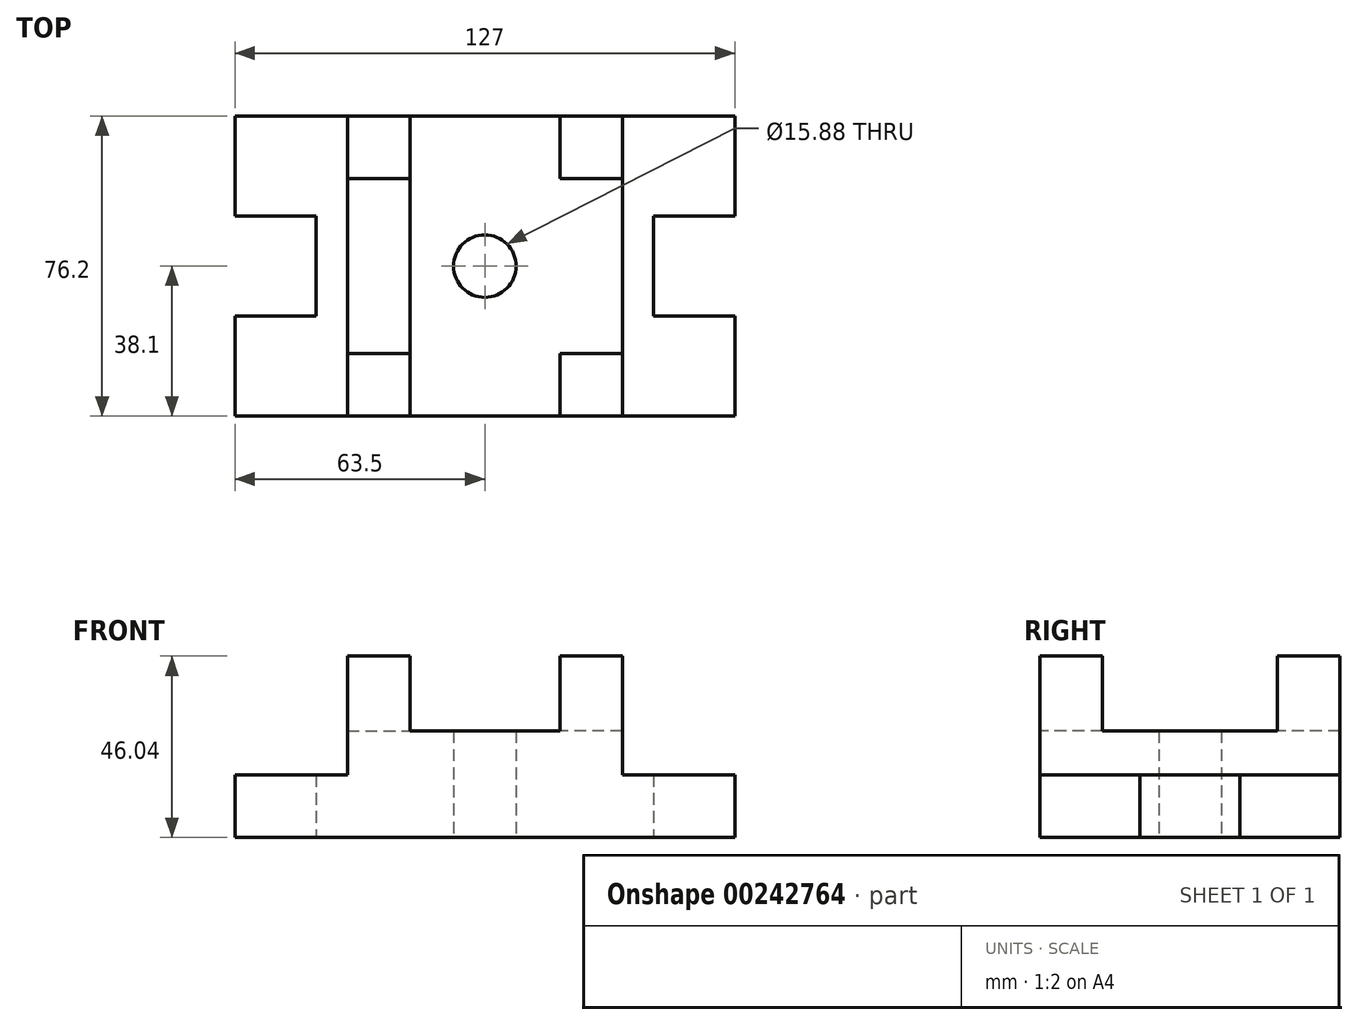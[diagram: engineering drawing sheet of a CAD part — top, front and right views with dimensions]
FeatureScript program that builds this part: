
annotation { "Feature Type Name" : "Feature", "Feature Type Description" : "" }
export const myFeature = defineFeature(function(context is Context, id is Id, definition is map)
    precondition{}
    {
        {
            var Q0;
            Q0=qCreatedBy(makeId("Top.planeOp"),FACE);
            var sketch = newSketch(context, id + "F0", { "sketchPlane" : qUnion([Q0])});
            skLineSegment(sketch, "E0.bottom", {"start": v(63.5, 38.1) * mm, "end": v(-63.5, 38.1) * mm});
            skLineSegment(sketch, "E0.top", {"start": v(63.5, -38.1) * mm, "end": v(-63.5, -38.1) * mm});
            skLineSegment(sketch, "E0.left", {"start": v(63.5, 38.1) * mm, "end": v(63.5, 12.7) * mm});
            skPoint(sketch, "E0.middle", {"position": v(0, 0) * mm});
            skLineSegment(sketch, "E1.bottom", {"start": v(-42.85, 12.7) * mm, "end": v(-63.5, 12.7) * mm});
            skLineSegment(sketch, "E1.top", {"start": v(-42.85, -12.7) * mm, "end": v(-63.5, -12.7) * mm});
            skLineSegment(sketch, "E1.left", {"start": v(-42.85, 12.7) * mm, "end": v(-42.85, -12.7) * mm});
            skPoint(sketch, "E1.middle", {"position": v(-53.17, 0) * mm});
            skLineSegment(sketch, "E2.bottom", {"start": v(63.5, 12.7) * mm, "end": v(42.85, 12.7) * mm});
            skLineSegment(sketch, "E2.top", {"start": v(63.5, -12.7) * mm, "end": v(42.85, -12.7) * mm});
            skPoint(sketch, "E2.middle", {"position": v(53.17, 0) * mm});
            skLineSegment(sketch, "E3", {"start": v(42.85, 12.7) * mm, "end": v(42.85, -12.7) * mm});
            skLineSegment(sketch, "E4.trimOffspring", {"start": v(63.5, -12.7) * mm, "end": v(63.5, -38.1) * mm});
            skLineSegment(sketch, "E5", {"start": v(-63.5, -12.7) * mm, "end": v(-63.5, -38.1) * mm});
            skLineSegment(sketch, "E6", {"start": v(-63.5, 38.1) * mm, "end": v(-63.5, 12.7) * mm});
            skSolve(sketch);
        }
        {
            var Q0;
            Q0=makeQuery(id+"F0.imprint","IMPRINT",FACE,{"disambiguationData":[TD([[makeQuery(id+"F0.imprint","IMPRINT",EDGE,{"derivedFrom":sQuery(id+"F0.wireOp",EDGE,"E0.bottom")}),1.0]])]});
            extrude(context, id + "F1", {"entities" : qUnion([Q0]), "depth" : 15.88 * mm});
        }
        {
            var Q0;
            Q0=makeQuery(id+"F1.opExtrude","CAP_FACE",FACE,{"disambiguationData":[OSD([sQuery(id+"F0.wireOp",EDGE,"E0.bottom"),sQuery(id+"F0.wireOp",EDGE,"E0.top"),sQuery(id+"F0.wireOp",EDGE,"E0.left"),sQuery(id+"F0.wireOp",EDGE,"E1.bottom"),sQuery(id+"F0.wireOp",EDGE,"E1.top"),sQuery(id+"F0.wireOp",EDGE,"E1.left"),sQuery(id+"F0.wireOp",EDGE,"E2.bottom"),sQuery(id+"F0.wireOp",EDGE,"E2.top"),sQuery(id+"F0.wireOp",EDGE,"E3"),sQuery(id+"F0.wireOp",EDGE,"E4.trimOffspring"),sQuery(id+"F0.wireOp",EDGE,"E5"),sQuery(id+"F0.wireOp",EDGE,"E6")])],"isStart":false});
            var sketch = newSketch(context, id + "F2", { "sketchPlane" : qUnion([Q0])});
            skLineSegment(sketch, "E7.bottom", {"start": v(34.93, 38.1) * mm, "end": v(-34.93, 38.1) * mm});
            skLineSegment(sketch, "E7.top", {"start": v(34.93, -38.1) * mm, "end": v(-34.92, -38.1) * mm});
            skLineSegment(sketch, "E7.left", {"start": v(34.93, 38.1) * mm, "end": v(34.93, -38.1) * mm});
            skLineSegment(sketch, "E7.right", {"start": v(-34.93, 38.1) * mm, "end": v(-34.92, -38.1) * mm});
            skPoint(sketch, "E7.middle", {"position": v(0, 0) * mm});
            skCircle(sketch, "E8", {"center": v(0, 0) * mm, "radius": 7.94 * mm});
            skSolve(sketch);
        }
        {
            var Q0;
            Q0=makeQuery(id+"F2.imprint","IMPRINT",FACE,{"disambiguationData":[TD([[makeQuery(id+"F2.imprint","IMPRINT",EDGE,{"derivedFrom":sQuery(id+"F2.wireOp",EDGE,"E7.bottom")}),1.0]])]});
            extrude(context, id + "F3", {"entities" : qUnion([Q0]), "operationType" : NewBodyOperationType.ADD, "depth" : 11.1 * mm});
        }
        {
            var Q0;
            Q0=makeQuery(id+"F3.boolean.opBoolean","SPLIT",FACE,{"disambiguationData":[TD([makeQuery(id+"F3.opExtrude","SWEPT_FACE",FACE,{"disambiguationData":[OSD([sQuery(id+"F2.wireOp",EDGE,"E8")])]})])],"derivedFrom":makeQuery(id+"F1.opExtrude","CAP_FACE",FACE,{"disambiguationData":[OSD([sQuery(id+"F0.wireOp",EDGE,"E0.bottom"),sQuery(id+"F0.wireOp",EDGE,"E0.top"),sQuery(id+"F0.wireOp",EDGE,"E0.left"),sQuery(id+"F0.wireOp",EDGE,"E1.bottom"),sQuery(id+"F0.wireOp",EDGE,"E1.top"),sQuery(id+"F0.wireOp",EDGE,"E1.left"),sQuery(id+"F0.wireOp",EDGE,"E2.bottom"),sQuery(id+"F0.wireOp",EDGE,"E2.top"),sQuery(id+"F0.wireOp",EDGE,"E3"),sQuery(id+"F0.wireOp",EDGE,"E4.trimOffspring"),sQuery(id+"F0.wireOp",EDGE,"E5"),sQuery(id+"F0.wireOp",EDGE,"E6")])],"isStart":false})});
            extrude(context, id + "F4", {"entities" : qUnion([Q0]), "operationType" : NewBodyOperationType.REMOVE, "endBound" : BoundingType.THROUGH_ALL, "oppositeDirection" : true, "depth" : 25.4 * mm});
        }
        {
            var Q0;
            Q0=makeQuery(id+"F3.opExtrude","CAP_FACE",FACE,{"disambiguationData":[OSD([sQuery(id+"F2.wireOp",EDGE,"E7.bottom"),sQuery(id+"F2.wireOp",EDGE,"E7.top"),sQuery(id+"F2.wireOp",EDGE,"E7.left"),sQuery(id+"F2.wireOp",EDGE,"E7.right"),sQuery(id+"F2.wireOp",EDGE,"E8")])],"isStart":false});
            var sketch = newSketch(context, id + "F5", { "sketchPlane" : qUnion([Q0])});
            skLineSegment(sketch, "E9.bottom", {"start": v(34.93, -38.1) * mm, "end": v(19.05, -38.1) * mm});
            skLineSegment(sketch, "E9.top", {"start": v(34.93, -22.22) * mm, "end": v(19.05, -22.22) * mm});
            skLineSegment(sketch, "E9.left", {"start": v(34.93, -38.1) * mm, "end": v(34.93, -22.22) * mm});
            skLineSegment(sketch, "E9.right", {"start": v(19.05, -38.1) * mm, "end": v(19.05, -22.23) * mm});
            skLineSegment(sketch, "E10.bottom", {"start": v(34.93, 38.1) * mm, "end": v(19.05, 38.1) * mm});
            skLineSegment(sketch, "E10.top", {"start": v(34.93, 22.23) * mm, "end": v(19.05, 22.23) * mm});
            skLineSegment(sketch, "E10.left", {"start": v(34.93, 38.1) * mm, "end": v(34.93, 22.23) * mm});
            skLineSegment(sketch, "E10.right", {"start": v(19.05, 38.1) * mm, "end": v(19.05, 22.23) * mm});
            skLineSegment(sketch, "E11.bottom", {"start": v(19.05, 22.23) * mm, "end": v(34.93, 22.23) * mm});
            skLineSegment(sketch, "E11.top", {"start": v(19.05, -22.22) * mm, "end": v(34.93, -22.22) * mm});
            skLineSegment(sketch, "E11.left", {"start": v(19.05, 22.23) * mm, "end": v(19.05, -22.23) * mm});
            skLineSegment(sketch, "E11.right", {"start": v(34.93, 22.23) * mm, "end": v(34.93, -22.23) * mm});
            skLineSegment(sketch, "E12.bottom", {"start": v(-34.93, 38.1) * mm, "end": v(-19.05, 38.1) * mm});
            skLineSegment(sketch, "E12.top", {"start": v(-34.93, 22.23) * mm, "end": v(-19.05, 22.23) * mm});
            skLineSegment(sketch, "E12.left", {"start": v(-34.93, 38.1) * mm, "end": v(-34.93, 22.23) * mm});
            skLineSegment(sketch, "E12.right", {"start": v(-19.05, 38.1) * mm, "end": v(-19.05, 22.23) * mm});
            skLineSegment(sketch, "E13.top", {"start": v(-34.93, -22.22) * mm, "end": v(-19.05, -22.22) * mm});
            skLineSegment(sketch, "E13.left", {"start": v(-34.93, 22.23) * mm, "end": v(-34.93, -22.22) * mm});
            skLineSegment(sketch, "E13.right", {"start": v(-19.05, 22.23) * mm, "end": v(-19.05, -22.22) * mm});
            skLineSegment(sketch, "E14.top", {"start": v(-34.93, -38.1) * mm, "end": v(-19.05, -38.1) * mm});
            skLineSegment(sketch, "E14.left", {"start": v(-34.93, -22.22) * mm, "end": v(-34.93, -38.1) * mm});
            skLineSegment(sketch, "E14.right", {"start": v(-19.05, -22.22) * mm, "end": v(-19.05, -38.1) * mm});
            skSolve(sketch);
        }
        {
            var Q0;
            Q0=makeQuery(id+"F5.imprint","IMPRINT",FACE,{"disambiguationData":[TD([[makeQuery(id+"F5.imprint","IMPRINT",EDGE,{"derivedFrom":sQuery(id+"F5.wireOp",EDGE,"E12.bottom")}),1.0]])]});
            var Q1;
            Q1=makeQuery(id+"F5.imprint","IMPRINT",FACE,{"disambiguationData":[TD([[makeQuery(id+"F5.imprint","IMPRINT",EDGE,{"derivedFrom":sQuery(id+"F5.wireOp",EDGE,"E10.bottom")}),1.0]])]});
            var Q2;
            Q2=makeQuery(id+"F5.imprint","IMPRINT",FACE,{"disambiguationData":[TD([[makeQuery(id+"F5.imprint","IMPRINT",EDGE,{"derivedFrom":sQuery(id+"F5.wireOp",EDGE,"E9.bottom")}),-1.0]])]});
            var Q3;
            Q3=makeQuery(id+"F5.imprint","IMPRINT",FACE,{"disambiguationData":[TD([[makeQuery(id+"F5.imprint","IMPRINT",EDGE,{"derivedFrom":sQuery(id+"F5.wireOp",EDGE,"E13.top")}),-1.0]])]});
            extrude(context, id + "F6", {"entities" : qUnion([Q0, Q1, Q2, Q3]), "operationType" : NewBodyOperationType.ADD, "depth" : 19.05 * mm});
        }
        {
            var Q0;
            Q0=makeQuery(id+"F3.opExtrude","CAP_FACE",FACE,{"disambiguationData":[OSD([sQuery(id+"F2.wireOp",EDGE,"E7.bottom"),sQuery(id+"F2.wireOp",EDGE,"E7.top"),sQuery(id+"F2.wireOp",EDGE,"E7.left"),sQuery(id+"F2.wireOp",EDGE,"E7.right"),sQuery(id+"F2.wireOp",EDGE,"E8")])],"isStart":false});
            var sketch = newSketch(context, id + "F7", { "sketchPlane" : qUnion([Q0])});
            skLineSegment(sketch, "E15.bottom", {"start": v(-34.93, 22.23) * mm, "end": v(-19.05, 22.23) * mm});
            skLineSegment(sketch, "E15.top", {"start": v(-34.93, -22.22) * mm, "end": v(-19.05, -22.22) * mm});
            skLineSegment(sketch, "E15.left", {"start": v(-34.93, 22.23) * mm, "end": v(-34.93, -22.22) * mm});
            skLineSegment(sketch, "E15.right", {"start": v(-19.05, 22.23) * mm, "end": v(-19.05, -22.22) * mm});
            skLineSegment(sketch, "E16.bottom", {"start": v(19.05, 22.23) * mm, "end": v(34.93, 22.23) * mm});
            skLineSegment(sketch, "E16.top", {"start": v(19.05, -22.22) * mm, "end": v(34.93, -22.22) * mm});
            skLineSegment(sketch, "E16.left", {"start": v(19.05, 22.23) * mm, "end": v(19.05, -22.23) * mm});
            skLineSegment(sketch, "E16.right", {"start": v(34.93, 22.23) * mm, "end": v(34.93, -22.23) * mm});
            skSolve(sketch);
        }
        {
            var Q0;
            Q0=makeQuery(id+"F7.imprint","IMPRINT",FACE,{"disambiguationData":[TD([[makeQuery(id+"F7.imprint","IMPRINT",EDGE,{"derivedFrom":sQuery(id+"F7.wireOp",EDGE,"E16.bottom")}),-1.0]])]});
            var Q1;
            Q1=makeQuery(id+"F7.imprint","IMPRINT",FACE,{"disambiguationData":[TD([[makeQuery(id+"F7.imprint","IMPRINT",EDGE,{"derivedFrom":sQuery(id+"F7.wireOp",EDGE,"E15.bottom")}),-1.0]])]});
            extrude(context, id + "F8", {"entities" : qUnion([Q0, Q1]), "operationType" : NewBodyOperationType.ADD, "depth" : 3 / 203.2 * mm});
        }
    });
